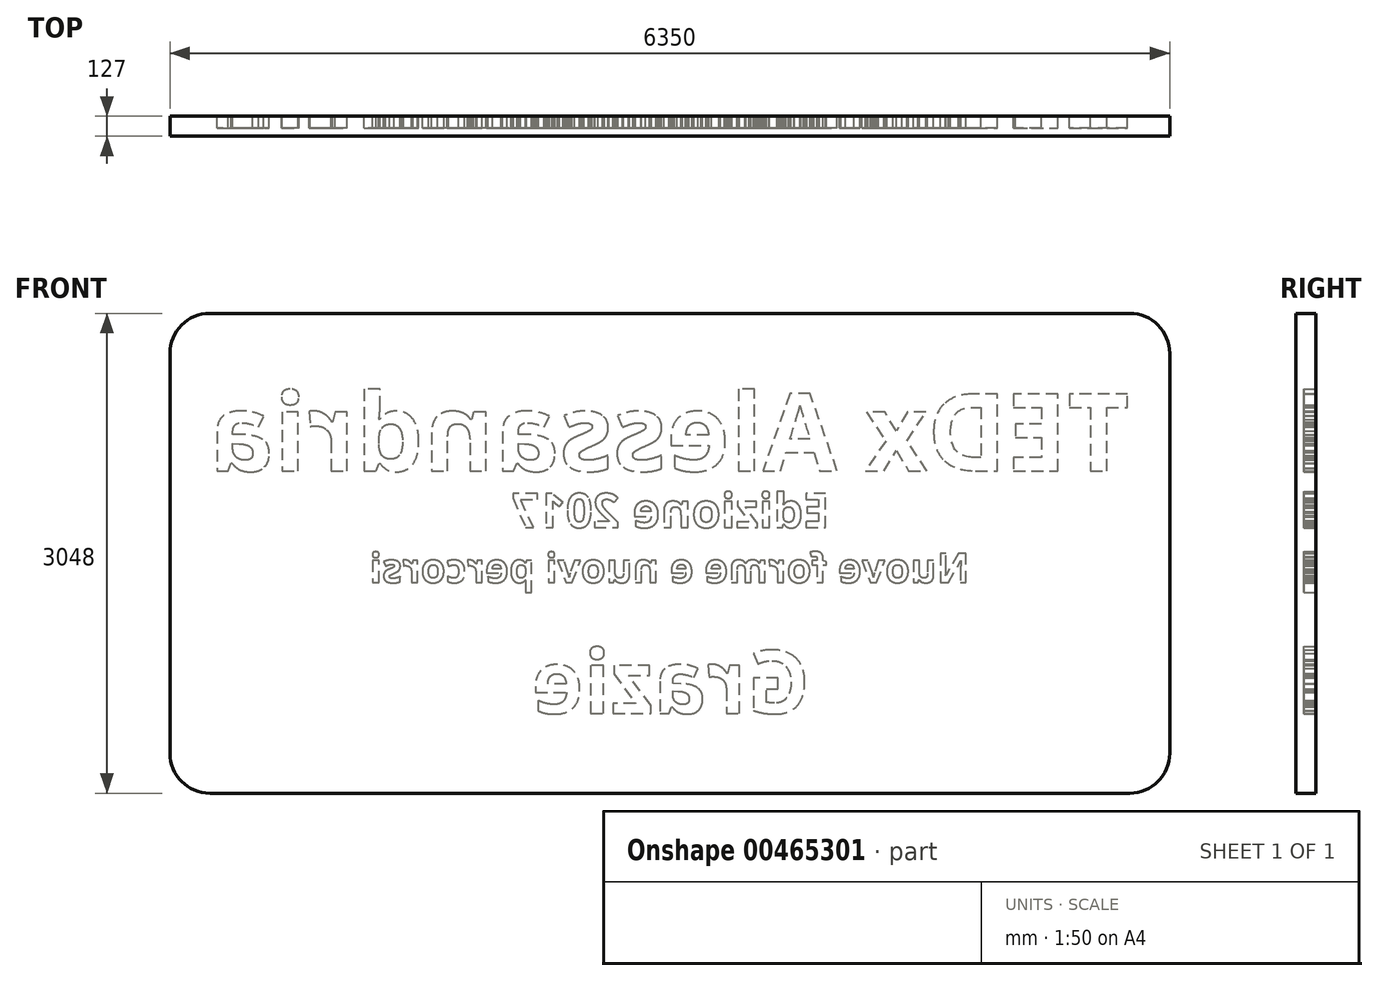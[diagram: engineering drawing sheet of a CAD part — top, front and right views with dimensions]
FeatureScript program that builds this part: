
annotation { "Feature Type Name" : "Feature", "Feature Type Description" : "" }
export const myFeature = defineFeature(function(context is Context, id is Id, definition is map)
    precondition{}
    {
        {
            var Q0;
            Q0=qCreatedBy(makeId("Front.planeOp"),FACE);
            var sketch = newSketch(context, id + "F0", { "sketchPlane" : qUnion([Q0])});
            skLineSegment(sketch, "E0.bottom", {"start": v(3175, 1524) * mm, "end": v(-3175, 1524) * mm});
            skLineSegment(sketch, "E0.top", {"start": v(3175, -1524) * mm, "end": v(-3175, -1524) * mm});
            skLineSegment(sketch, "E0.left", {"start": v(3175, 1524) * mm, "end": v(3175, -1524) * mm});
            skLineSegment(sketch, "E0.right", {"start": v(-3175, 1524) * mm, "end": v(-3175, -1524) * mm});
            skPoint(sketch, "E0.middle", {"position": v(0, 0) * mm});
            skSolve(sketch);
        }
        {
            var Q0;
            Q0=makeQuery(id+"F0.imprint","IMPRINT",FACE,{"disambiguationData":[TD([[makeQuery(id+"F0.imprint","IMPRINT",EDGE,{"derivedFrom":sQuery(id+"F0.wireOp",EDGE,"E0.bottom")}),1.0]])]});
            var Q1;
            Q1=sQuery(id+"F0.wireOp",EDGE,"E0.bottom");
            var Q2;
            Q2=sQuery(id+"F0.wireOp",EDGE,"E0.right");
            var Q3;
            Q3=sQuery(id+"F0.wireOp",EDGE,"E0.top");
            var Q4;
            Q4=sQuery(id+"F0.wireOp",EDGE,"E0.left");
            extrude(context, id + "F1", {"entities" : qUnion([Q0]), "surfaceEntities" : qUnion([Q1, Q2, Q3, Q4]), "depth" : 127 * mm});
        }
        {
            var Q0;
            Q0=makeQuery(id+"F1.opExtrude","CAP_FACE",FACE,{"disambiguationData":[OSD([sQuery(id+"F0.wireOp",EDGE,"E0.bottom"),sQuery(id+"F0.wireOp",EDGE,"E0.top"),sQuery(id+"F0.wireOp",EDGE,"E0.left"),sQuery(id+"F0.wireOp",EDGE,"E0.right")])],"isStart":true});
            var sketch = newSketch(context, id + "F2", { "sketchPlane" : qUnion([Q0])});
            skText(sketch, "E1", { "text": "TEDx Alessandria", "fontName": "OpenSans-Bold.ttf"});
            const initialGuessF2  = {"E1": [-2.921, 0.5237, 1, 0, 0.4923]};
            skSetInitialGuess(sketch, initialGuessF2);
            skSolve(sketch);
        }
        {
            var Q0;
            Q0 = qSketchRegion(id + "F2", true);
            extrude(context, id + "F3", {"entities" : qUnion([Q0]), "operationType" : NewBodyOperationType.REMOVE, "oppositeDirection" : true, "depth" : 76.2 * mm});
        }
        {
            var Q0;
            {var subQ0=sQuery(id+"F0.wireOp",EDGE,"E0.left");var subQ1=sQuery(id+"F0.wireOp",EDGE,"E0.bottom");var subQ2=sQuery(id+"F0.wireOp",EDGE,"E0.right");var subQ3=sQuery(id+"F0.wireOp",EDGE,"E0.top");Q0=makeQuery(id+"F3.boolean.opBoolean","SPLIT",FACE,{"disambiguationData":[TD([makeQuery(id+"F1.opExtrude","SWEPT_FACE",FACE,{"disambiguationData":[OSD([subQ1])]})])],"derivedFrom":makeQuery(id+"F1.opExtrude","CAP_FACE",FACE,{"disambiguationData":[OSD([subQ1,subQ3,subQ0,subQ2])],"isStart":true})});}
            var sketch = newSketch(context, id + "F4", { "sketchPlane" : qUnion([Q0])});
            skText(sketch, "E2", { "text": "Grazie", "fontName": "OpenSans-Bold.ttf"});
            const initialGuessF4  = {"E2": [-0.889, -1.016, 1, 0, 0.40158]};
            skSetInitialGuess(sketch, initialGuessF4);
            skSolve(sketch);
        }
        {
            var Q0;
            Q0 = qSketchRegion(id + "F4", true);
            extrude(context, id + "F5", {"entities" : qUnion([Q0]), "operationType" : NewBodyOperationType.REMOVE, "oppositeDirection" : true, "depth" : 76.2 * mm});
        }
        {
            var Q0;
            Q0=makeQuery(id+"F1.opExtrude","SWEPT_EDGE",EDGE,{"disambiguationData":[OSD([sQuery(id+"F0.wireOp",EDGE,"E0.bottom"),sQuery(id+"F0.wireOp",EDGE,"E0.right")])]});
            var Q1;
            Q1=makeQuery(id+"F1.opExtrude","SWEPT_EDGE",EDGE,{"disambiguationData":[OSD([sQuery(id+"F0.wireOp",EDGE,"E0.bottom"),sQuery(id+"F0.wireOp",EDGE,"E0.left")])]});
            var Q2;
            Q2=makeQuery(id+"F1.opExtrude","SWEPT_EDGE",EDGE,{"disambiguationData":[OSD([sQuery(id+"F0.wireOp",EDGE,"E0.top"),sQuery(id+"F0.wireOp",EDGE,"E0.left")])]});
            var Q3;
            Q3=makeQuery(id+"F1.opExtrude","SWEPT_EDGE",EDGE,{"disambiguationData":[OSD([sQuery(id+"F0.wireOp",EDGE,"E0.top"),sQuery(id+"F0.wireOp",EDGE,"E0.right")])]});
            fillet(context, id + "F6", {"entities" : qUnion([Q0, Q1, Q2, Q3]), "radius" : 254 * mm, "tangentPropagation" : true, "allowEdgeOverflow" : false});
        }
        {
            var Q0;
            {var subQ122=sQuery(id+"F0.wireOp",EDGE,"E0.bottom");var subQ123=makeQuery(id+"F1.opExtrude","SWEPT_FACE",FACE,{"disambiguationData":[OSD([subQ122])]});var subQ130=sQuery(id+"F0.wireOp",EDGE,"E0.right");var subQ138=sQuery(id+"F0.wireOp",EDGE,"E0.top");var subQ146=sQuery(id+"F0.wireOp",EDGE,"E0.left");Q0=makeQuery(id+"F5.boolean.opBoolean","SPLIT",FACE,{"disambiguationData":[TD([subQ123])],"derivedFrom":makeQuery(id+"F3.boolean.opBoolean","SPLIT",FACE,{"disambiguationData":[TD([subQ123])],"derivedFrom":makeQuery(id+"F1.opExtrude","CAP_FACE",FACE,{"disambiguationData":[OSD([subQ122,subQ138,subQ146,subQ130])],"isStart":true})})});}
            var sketch = newSketch(context, id + "F7", { "sketchPlane" : qUnion([Q0])});
            skText(sketch, "E3", { "text": "Edizione 2017", "fontName": "OpenSans-Bold.ttf"});
            const initialGuessF7  = {"E3": [-1.016, 0.16375, 1, 0, 0.21725]};
            skSetInitialGuess(sketch, initialGuessF7);
            skSolve(sketch);
        }
        {
            var Q0;
            Q0 = qSketchRegion(id + "F7", true);
            extrude(context, id + "F8", {"entities" : qUnion([Q0]), "operationType" : NewBodyOperationType.REMOVE, "oppositeDirection" : true, "depth" : 76.2 * mm});
        }
        {
            var Q0;
            {var subQ295=sQuery(id+"F0.wireOp",EDGE,"E0.left");var subQ296=sQuery(id+"F0.wireOp",EDGE,"E0.bottom");var subQ362=sQuery(id+"F0.wireOp",EDGE,"E0.top");var subQ374=sQuery(id+"F0.wireOp",EDGE,"E0.right");var subQ389=makeQuery(id+"F1.opExtrude","SWEPT_FACE",FACE,{"disambiguationData":[OSD([subQ296])]});Q0=makeQuery(id+"F8.boolean.opBoolean","SPLIT",FACE,{"disambiguationData":[TD([subQ389])],"derivedFrom":makeQuery(id+"F5.boolean.opBoolean","SPLIT",FACE,{"disambiguationData":[TD([subQ389])],"derivedFrom":makeQuery(id+"F3.boolean.opBoolean","SPLIT",FACE,{"disambiguationData":[TD([subQ389])],"derivedFrom":makeQuery(id+"F1.opExtrude","CAP_FACE",FACE,{"disambiguationData":[OSD([subQ296,subQ362,subQ295,subQ374])],"isStart":true})})})});}
            var sketch = newSketch(context, id + "F9", { "sketchPlane" : qUnion([Q0])});
            skText(sketch, "E4", { "text": "Nuove forme e nuovi percorsi", "fontName": "OpenSans-Bold.ttf"});
            const initialGuessF9  = {"E4": [-1.905, -0.1856, 1, 0, 0.1856]};
            skSetInitialGuess(sketch, initialGuessF9);
            skSolve(sketch);
        }
        {
            var Q0;
            Q0 = qSketchRegion(id + "F9", true);
            extrude(context, id + "F10", {"entities" : qUnion([Q0]), "operationType" : NewBodyOperationType.REMOVE, "oppositeDirection" : true, "depth" : 76.2 * mm});
        }
    });
